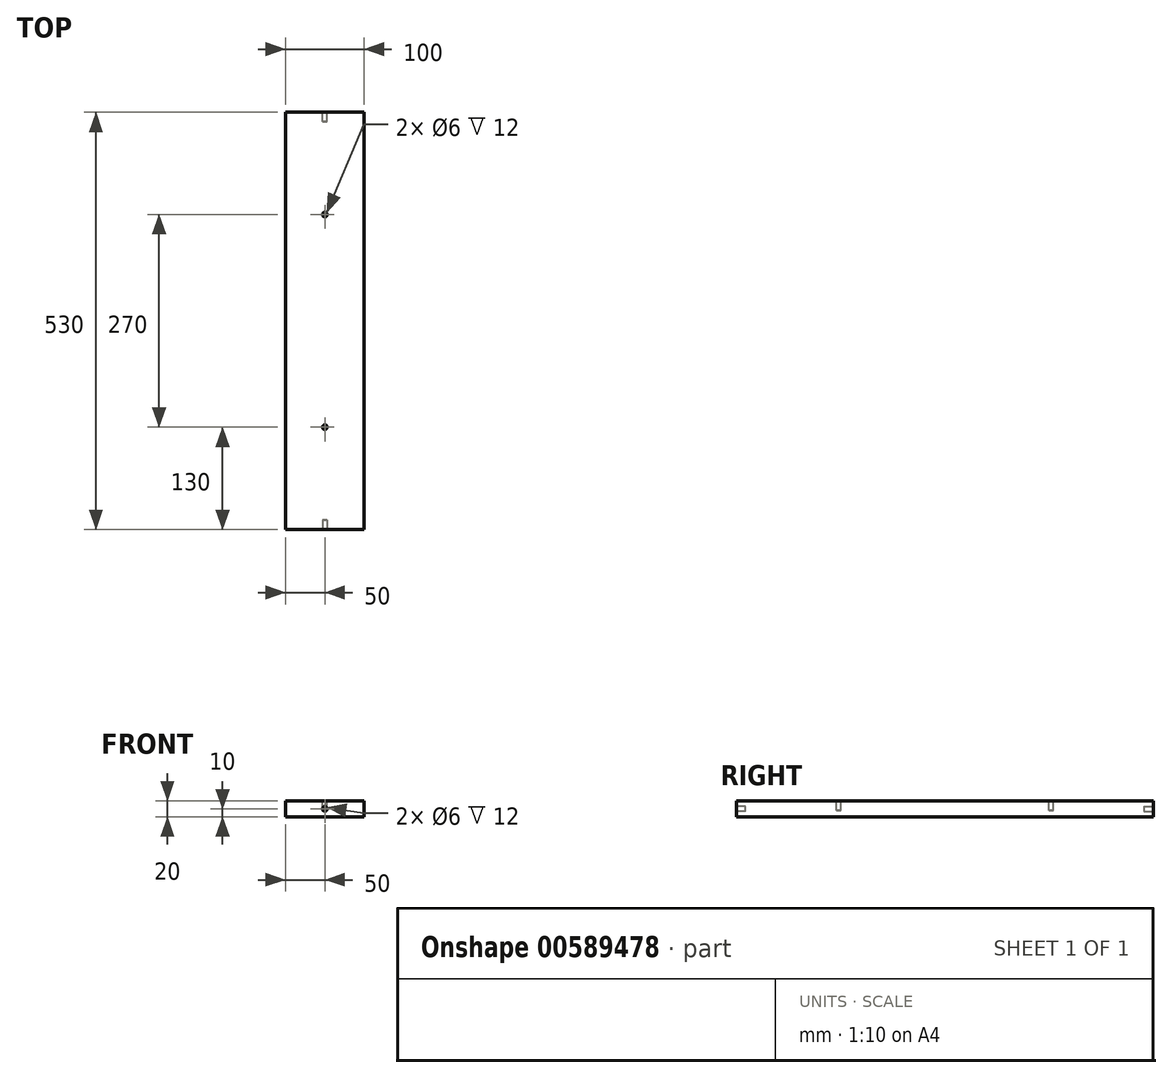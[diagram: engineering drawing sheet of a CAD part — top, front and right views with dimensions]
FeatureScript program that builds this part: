
annotation { "Feature Type Name" : "Feature", "Feature Type Description" : "" }
export const myFeature = defineFeature(function(context is Context, id is Id, definition is map)
    precondition{}
    {
        {
            var Q0;
            Q0=qCreatedBy(makeId("Top.planeOp"),FACE);
            var sketch = newSketch(context, id + "F0", { "sketchPlane" : qUnion([Q0])});
            skLineSegment(sketch, "E0.bottom", {"start": v(0, 0) * mm, "end": v(100, 0) * mm});
            skLineSegment(sketch, "E0.top", {"start": v(0, 530) * mm, "end": v(100, 530) * mm});
            skLineSegment(sketch, "E0.left", {"start": v(0, 0) * mm, "end": v(0, 530) * mm});
            skLineSegment(sketch, "E0.right", {"start": v(100, 0) * mm, "end": v(100, 530) * mm});
            skSolve(sketch);
        }
        {
            var Q0;
            Q0=makeQuery(id+"F0.imprint","IMPRINT",FACE,{"disambiguationData":[TD([[makeQuery(id+"F0.imprint","IMPRINT",EDGE,{"derivedFrom":sQuery(id+"F0.wireOp",EDGE,"E0.bottom")}),1.0]])]});
            extrude(context, id + "F1", {"entities" : qUnion([Q0]), "depth" : 20 * mm, "offsetDistance" : 25 * mm});
        }
        {
            var Q0;
            Q0=makeQuery(id+"F1.opExtrude","CAP_FACE",FACE,{"disambiguationData":[OSD([sQuery(id+"F0.wireOp",EDGE,"E0.bottom"),sQuery(id+"F0.wireOp",EDGE,"E0.top"),sQuery(id+"F0.wireOp",EDGE,"E0.left"),sQuery(id+"F0.wireOp",EDGE,"E0.right")])],"isStart":false});
            var sketch = newSketch(context, id + "F2", { "sketchPlane" : qUnion([Q0])});
            skCircle(sketch, "E1", {"center": v(50, 130) * mm, "radius": 3 * mm});
            skPoint(sketch, "E1.centerSnap0", {"position": v(50, 0) * mm});
            skSolve(sketch);
        }
        {
            var Q0;
            Q0=makeQuery(id+"F2.imprint","IMPRINT",FACE,{"disambiguationData":[TD([[makeQuery(id+"F2.imprint","IMPRINT",EDGE,{"derivedFrom":sQuery(id+"F2.wireOp",EDGE,"E1")}),1.0]])]});
            extrude(context, id + "F3", {"entities" : qUnion([Q0]), "operationType" : NewBodyOperationType.REMOVE, "oppositeDirection" : true, "depth" : 12 * mm, "offsetDistance" : 25 * mm});
        }
        {
            var Q0;
            Q0=makeQuery(id+"F1.opExtrude","SWEPT_FACE",FACE,{"disambiguationData":[OSD([sQuery(id+"F0.wireOp",EDGE,"E0.bottom")])]});
            var sketch = newSketch(context, id + "F4", { "sketchPlane" : qUnion([Q0])});
            skCircle(sketch, "E2", {"center": v(50, 10) * mm, "radius": 3 * mm});
            skPoint(sketch, "E2.centerSnap0", {"position": v(0, 10) * mm});
            skPoint(sketch, "E2.centerSnap1", {"position": v(50, 20) * mm});
            skSolve(sketch);
        }
        {
            var Q0;
            Q0=makeQuery(id+"F4.imprint","IMPRINT",FACE,{"disambiguationData":[TD([[makeQuery(id+"F4.imprint","IMPRINT",EDGE,{"derivedFrom":sQuery(id+"F4.wireOp",EDGE,"E2")}),1.0]])]});
            extrude(context, id + "F5", {"entities" : qUnion([Q0]), "operationType" : NewBodyOperationType.REMOVE, "oppositeDirection" : true, "depth" : 12 * mm, "offsetDistance" : 25 * mm});
        }
        {
            var Q0;
            Q0=makeQuery(id+"F1.opExtrude","SWEPT_FACE",FACE,{"disambiguationData":[OSD([sQuery(id+"F0.wireOp",EDGE,"E0.top")])]});
            var sketch = newSketch(context, id + "F6", { "sketchPlane" : qUnion([Q0])});
            skCircle(sketch, "E3.0", {"center": v(-50, 10) * mm, "radius": 3 * mm});
            skSolve(sketch);
        }
        {
            var Q0;
            Q0=makeQuery(id+"F6.imprint","IMPRINT",FACE,{"disambiguationData":[TD([[makeQuery(id+"F6.imprint","IMPRINT",EDGE,{"derivedFrom":sQuery(id+"F6.wireOp",EDGE,"E3.0")}),1.0]])]});
            extrude(context, id + "F7", {"entities" : qUnion([Q0]), "operationType" : NewBodyOperationType.REMOVE, "oppositeDirection" : true, "depth" : 12 * mm, "offsetDistance" : 25 * mm});
        }
        {
            var Q0;
            Q0=makeQuery(id+"F1.opExtrude","CAP_FACE",FACE,{"disambiguationData":[OSD([sQuery(id+"F0.wireOp",EDGE,"E0.bottom"),sQuery(id+"F0.wireOp",EDGE,"E0.top"),sQuery(id+"F0.wireOp",EDGE,"E0.left"),sQuery(id+"F0.wireOp",EDGE,"E0.right")])],"isStart":false});
            var sketch = newSketch(context, id + "F8", { "sketchPlane" : qUnion([Q0])});
            skCircle(sketch, "E4", {"center": v(50, 400) * mm, "radius": 3 * mm});
            skPoint(sketch, "E4.centerSnap0", {"position": v(50, 530) * mm});
            skSolve(sketch);
        }
        {
            var Q0;
            Q0=makeQuery(id+"F8.imprint","IMPRINT",FACE,{"disambiguationData":[TD([[makeQuery(id+"F8.imprint","IMPRINT",EDGE,{"derivedFrom":sQuery(id+"F8.wireOp",EDGE,"E4")}),1.0]])]});
            extrude(context, id + "F9", {"entities" : qUnion([Q0]), "operationType" : NewBodyOperationType.REMOVE, "oppositeDirection" : true, "depth" : 12 * mm, "offsetDistance" : 25 * mm});
        }
    });
